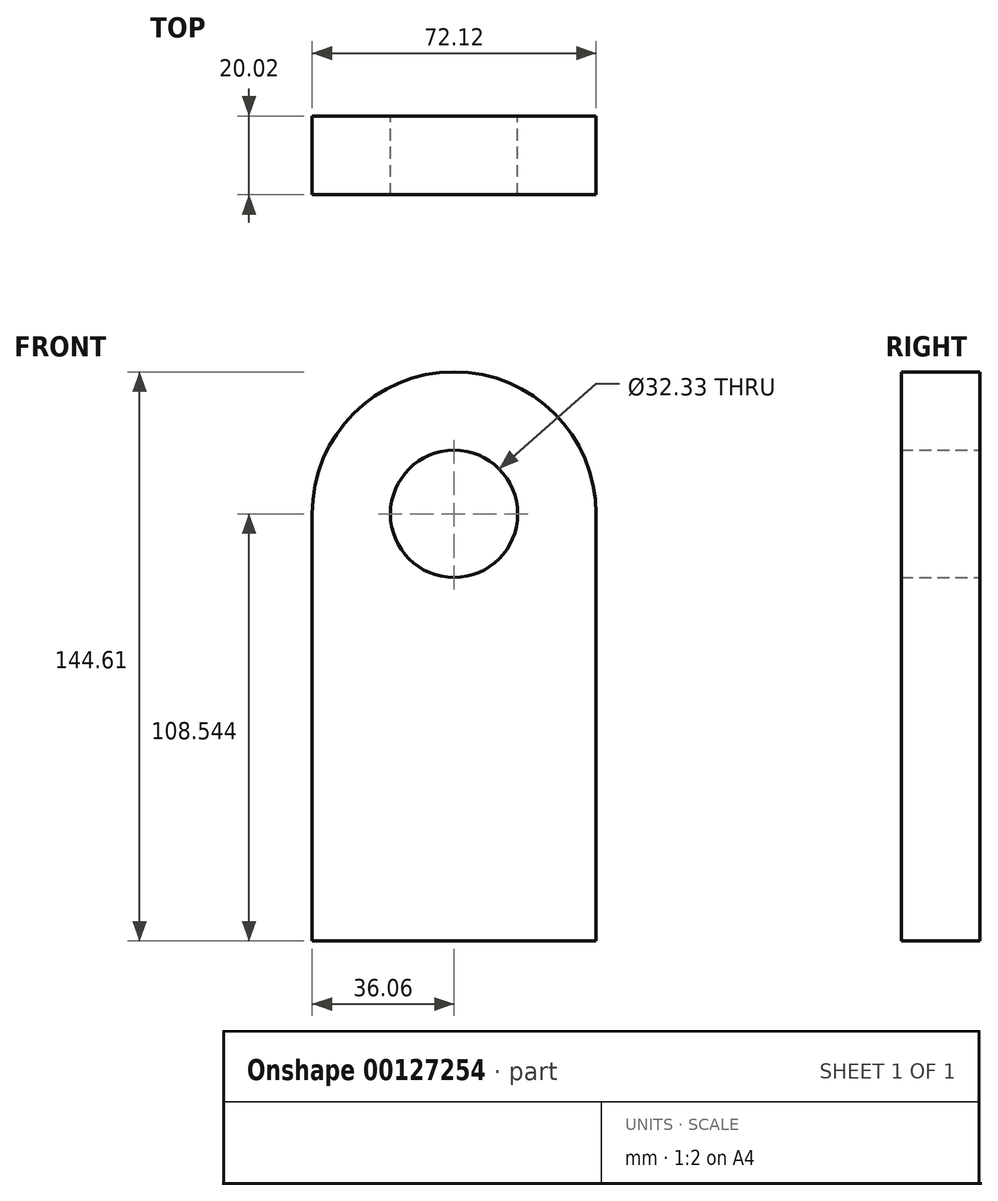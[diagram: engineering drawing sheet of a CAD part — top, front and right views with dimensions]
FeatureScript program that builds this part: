
annotation { "Feature Type Name" : "Feature", "Feature Type Description" : "" }
export const myFeature = defineFeature(function(context is Context, id is Id, definition is map)
    precondition{}
    {
        {
            var Q0;
            Q0=qCreatedBy(makeId("Front.planeOp"),FACE);
            var sketch = newSketch(context, id + "F0", { "sketchPlane" : qUnion([Q0])});
            skLineSegment(sketch, "E0.bottom", {"start": v(36.06, -54.27) * mm, "end": v(-36.06, -54.27) * mm});
            skLineSegment(sketch, "E0.left", {"start": v(36.06, -54.27) * mm, "end": v(36.06, 54.27) * mm});
            skLineSegment(sketch, "E0.right", {"start": v(-36.06, -54.27) * mm, "end": v(-36.06, 54.27) * mm});
            skPoint(sketch, "E0.middle", {"position": v(0, 0) * mm});
            skArc(sketch, "E1", {"start": v(36.06, 54.27) * mm, "mid": v(0, 90.34) * mm, "end": v(-36.06, 54.27) * mm});
            skCircle(sketch, "E2", {"center": v(0, 54.27) * mm, "radius": 16.16 * mm});
            skSolve(sketch);
        }
        {
            var Q0;
            Q0=makeQuery(id+"F0.imprint","IMPRINT",FACE,{"disambiguationData":[TD([[makeQuery(id+"F0.imprint","IMPRINT",EDGE,{"derivedFrom":sQuery(id+"F0.wireOp",EDGE,"E0.bottom")}),-1.0]])]});
            extrude(context, id + "F1", {"entities" : qUnion([Q0]), "depth" : 20.02 * mm});
        }
    });
